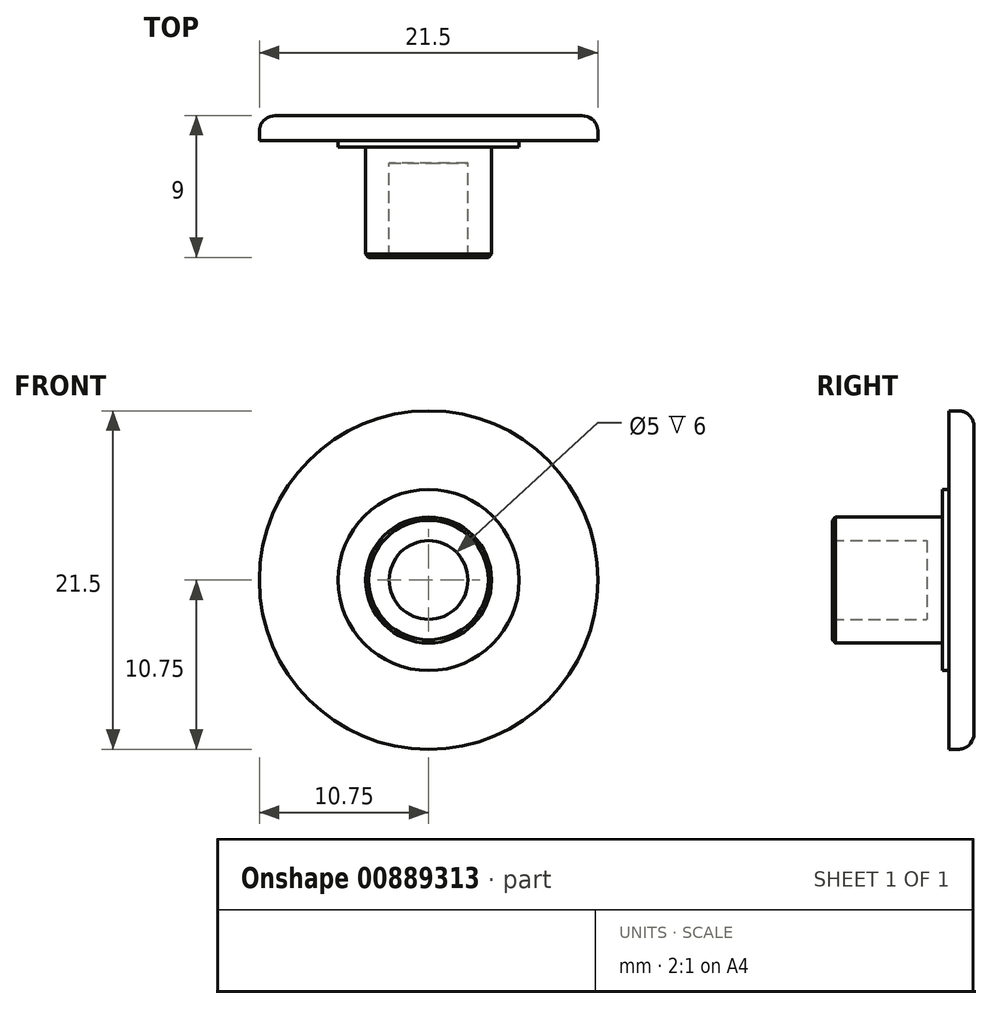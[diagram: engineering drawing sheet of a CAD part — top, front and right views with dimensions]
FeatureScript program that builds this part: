
annotation { "Feature Type Name" : "Feature", "Feature Type Description" : "" }
export const myFeature = defineFeature(function(context is Context, id is Id, definition is map)
    precondition{}
    {
        {
            var Q0;
            Q0=qCreatedBy(makeId("Top.planeOp"),FACE);
            var sketch = newSketch(context, id + "F0", { "sketchPlane" : qUnion([Q0])});
            skLineSegment(sketch, "E0", {"start": v(0, 9.69) * mm, "end": v(0, 0) * mm, "construction": true});
            skLineSegment(sketch, "E1", {"start": v(0, 0) * mm, "end": v(12.23, 0) * mm, "construction": true});
            skLineSegment(sketch, "E2", {"start": v(2.5, 0) * mm, "end": v(2.5, 6) * mm});
            skLineSegment(sketch, "E3", {"start": v(2.5, 6) * mm, "end": v(0, 6) * mm});
            skLineSegment(sketch, "E4", {"start": v(0, 6) * mm, "end": v(0, 9) * mm});
            skLineSegment(sketch, "E5", {"start": v(0, 9) * mm, "end": v(10.75, 9) * mm});
            skLineSegment(sketch, "E6", {"start": v(10.75, 9) * mm, "end": v(10.75, 7.4) * mm});
            skLineSegment(sketch, "E7", {"start": v(10.75, 7.4) * mm, "end": v(5.75, 7.4) * mm});
            skLineSegment(sketch, "E8", {"start": v(5.75, 7.4) * mm, "end": v(5.75, 7) * mm});
            skLineSegment(sketch, "E9", {"start": v(5.75, 7) * mm, "end": v(4, 7) * mm});
            skLineSegment(sketch, "E10", {"start": v(4, 7) * mm, "end": v(4, 0) * mm});
            skLineSegment(sketch, "E11", {"start": v(4, 0) * mm, "end": v(2.5, 0) * mm});
            skSolve(sketch);
        }
        {
            var Q0;
            Q0=makeQuery(id+"F0.imprint","IMPRINT",FACE,{"disambiguationData":[TD([[makeQuery(id+"F0.imprint","IMPRINT",EDGE,{"derivedFrom":sQuery(id+"F0.wireOp",EDGE,"E2")}),-1.0]])]});
            var Q1;
            Q1=sQuery(id+"F0.wireOp",EDGE,"E0");
            revolve(context, id + "F1", {"surfaceOperationType" : NewSurfaceOperationType.NEW, "entities" : qUnion([Q0]), "axis" : qUnion([Q1]), "revolveType" : RevolveType.FULL});
        }
        {
            var Q0;
            Q0=makeQuery(id+"F1.opRevolve","SWEPT_EDGE",EDGE,{"disambiguationData":[OSD([sQuery(id+"F0.wireOp",EDGE,"E10"),sQuery(id+"F0.wireOp",EDGE,"E11")])]});
            chamfer(context, id + "F2", {"entities" : qUnion([Q0]), "width" : .2 * mm, "tangentPropagation" : true});
        }
        {
            var Q0;
            Q0=makeQuery(id+"F1.opRevolve","SWEPT_FACE",FACE,{"disambiguationData":[OSD([sQuery(id+"F0.wireOp",EDGE,"E5")])]});
            fillet(context, id + "F3", {"entities" : qUnion([Q0]), "radius" : 1 * mm, "tangentPropagation" : true, "allowEdgeOverflow" : false});
        }
    });
